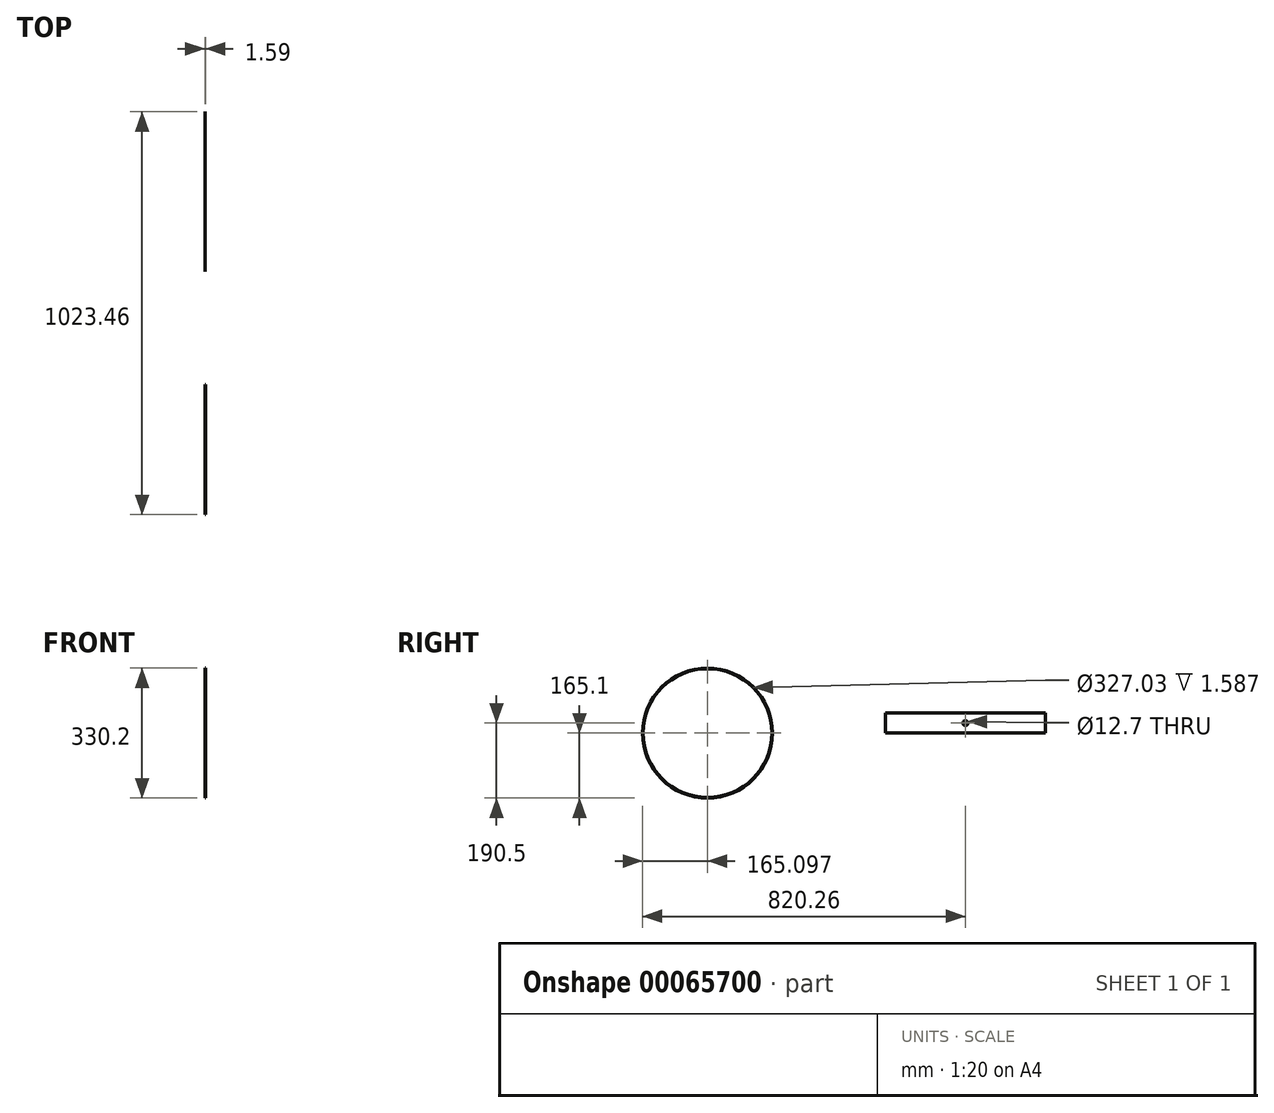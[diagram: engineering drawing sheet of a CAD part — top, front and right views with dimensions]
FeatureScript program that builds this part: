
annotation { "Feature Type Name" : "Feature", "Feature Type Description" : "" }
export const myFeature = defineFeature(function(context is Context, id is Id, definition is map)
    precondition{}
    {
        {
            var Q0;
            Q0=qCreatedBy(makeId("Right.planeOp"),FACE);
            var sketch = newSketch(context, id + "F0", { "sketchPlane" : qUnion([Q0])});
            skLineSegment(sketch, "E0.bottom", {"start": v(0, 0) * mm, "end": v(406.4, 0) * mm});
            skLineSegment(sketch, "E0.top", {"start": v(0, 50.8) * mm, "end": v(406.4, 50.8) * mm});
            skLineSegment(sketch, "E0.left", {"start": v(0, 0) * mm, "end": v(0, 50.8) * mm});
            skLineSegment(sketch, "E0.right", {"start": v(406.4, 0) * mm, "end": v(406.4, 50.8) * mm});
            skCircle(sketch, "E1", {"center": v(203.2, 25.4) * mm, "radius": 6.35 * mm});
            skPoint(sketch, "E1.centerSnap0", {"position": v(0, 25.4) * mm});
            skPoint(sketch, "E1.centerSnap1", {"position": v(203.2, 50.8) * mm});
            skSolve(sketch);
        }
        {
            var Q0;
            Q0=makeQuery(id+"F0.imprint","IMPRINT",FACE,{"disambiguationData":[TD([[makeQuery(id+"F0.imprint","IMPRINT",EDGE,{"derivedFrom":sQuery(id+"F0.wireOp",EDGE,"E0.bottom")}),1.0]])]});
            extrude(context, id + "F1", {"entities" : qUnion([Q0]), "depth" : 0.25 * mm});
        }
        {
            var Q0;
            Q0=qCreatedBy(makeId("Right.planeOp"),FACE);
            var sketch = newSketch(context, id + "F2", { "sketchPlane" : qUnion([Q0])});
            skCircle(sketch, "E2", {"center": v(-451.96, 0) * mm, "radius": 177.8 * mm});
            skCircle(sketch, "E3", {"center": v(-451.96, 0) * mm, "radius": 165.1 * mm});
            skCircle(sketch, "E4", {"center": v(-451.96, 0) * mm, "radius": 163.51 * mm});
            skSolve(sketch);
        }
        {
            var Q0;
            Q0=makeQuery(id+"F2.imprint","IMPRINT",FACE,{"disambiguationData":[TD([[makeQuery(id+"F2.imprint","IMPRINT",EDGE,{"derivedFrom":sQuery(id+"F2.wireOp",EDGE,"E3")}),1.0]])]});
            extrude(context, id + "F3", {"entities" : qUnion([Q0]), "depth" : 1.59 * mm});
        }
    });
